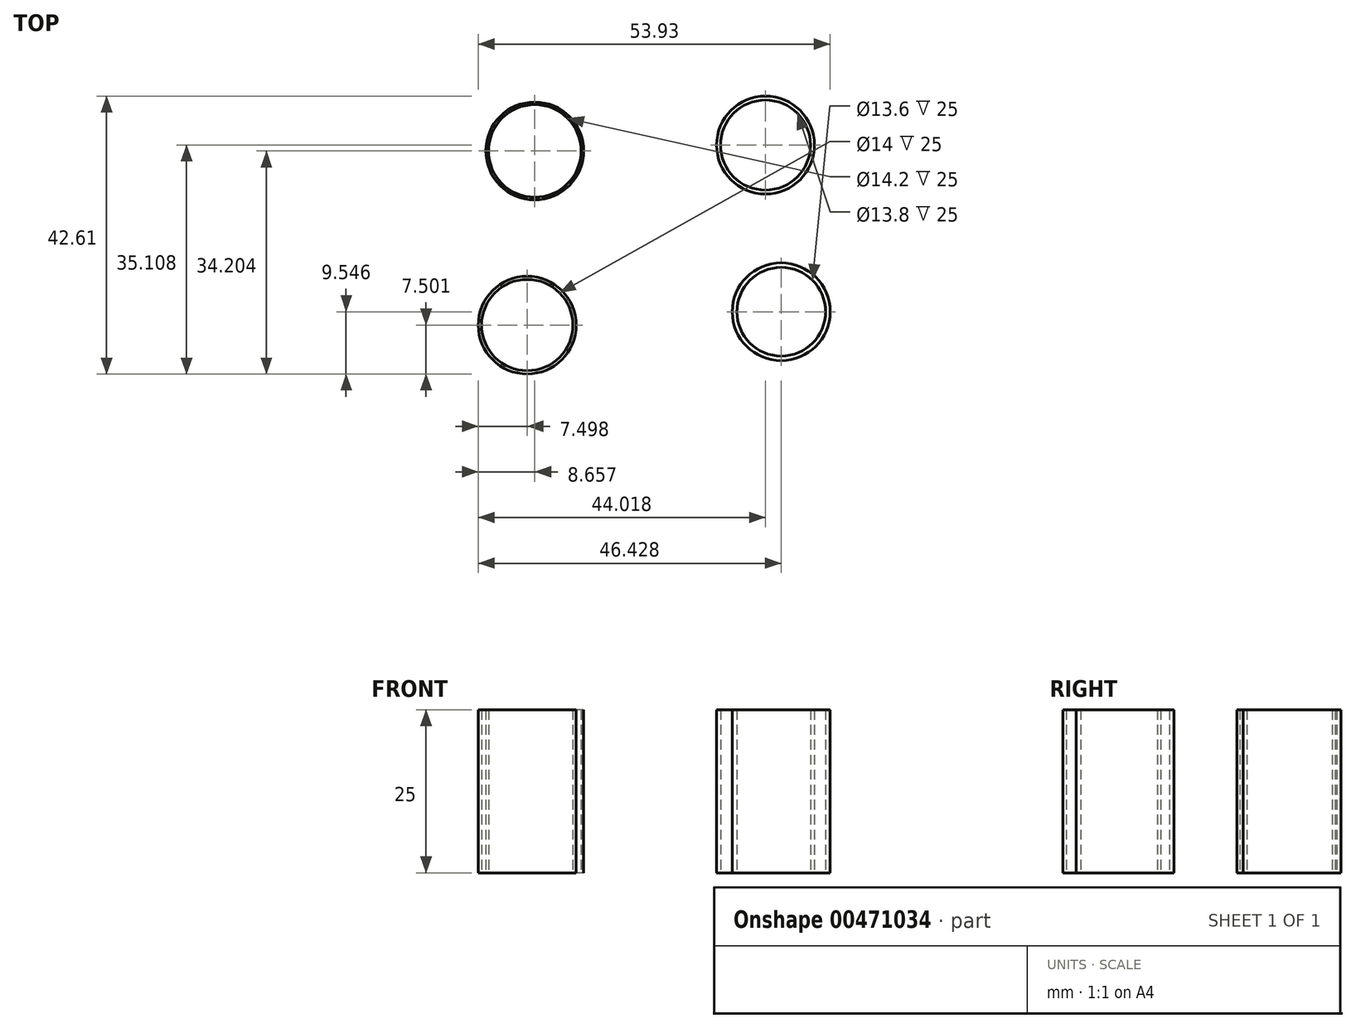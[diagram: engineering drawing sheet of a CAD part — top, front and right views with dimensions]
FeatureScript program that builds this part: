
annotation { "Feature Type Name" : "Feature", "Feature Type Description" : "" }
export const myFeature = defineFeature(function(context is Context, id is Id, definition is map)
    precondition{}
    {
        {
            var Q0;
            Q0=qCreatedBy(makeId("Top.planeOp"),FACE);
            var sketch = newSketch(context, id + "F0", { "sketchPlane" : qUnion([Q0])});
            skCircle(sketch, "E0", {"center": v(-62.66, 34.44) * mm, "radius": 7.1 * mm});
            skCircle(sketch, "E1", {"center": v(-62.66, 34.44) * mm, "radius": 7.5 * mm});
            skCircle(sketch, "E2", {"center": v(-63.82, 7.74) * mm, "radius": 7.5 * mm});
            skCircle(sketch, "E3", {"center": v(-63.82, 7.74) * mm, "radius": 7 * mm});
            skCircle(sketch, "E4", {"center": v(-27.3, 35.35) * mm, "radius": 6.9 * mm});
            skCircle(sketch, "E5", {"center": v(-27.3, 35.35) * mm, "radius": 7.5 * mm});
            skCircle(sketch, "E6", {"center": v(-24.9, 9.79) * mm, "radius": 7.5 * mm});
            skCircle(sketch, "E7", {"center": v(-24.9, 9.79) * mm, "radius": 6.8 * mm});
            skSolve(sketch);
        }
        {
            var Q0;
            Q0=makeQuery(id+"F0.imprint","IMPRINT",FACE,{"disambiguationData":[TD([[makeQuery(id+"F0.imprint","IMPRINT",EDGE,{"derivedFrom":sQuery(id+"F0.wireOp",EDGE,"E0")}),-1.0]])]});
            var Q1;
            Q1=makeQuery(id+"F0.imprint","IMPRINT",FACE,{"disambiguationData":[TD([[makeQuery(id+"F0.imprint","IMPRINT",EDGE,{"derivedFrom":sQuery(id+"F0.wireOp",EDGE,"E2")}),1.0]])]});
            var Q2;
            Q2=makeQuery(id+"F0.imprint","IMPRINT",FACE,{"disambiguationData":[TD([[makeQuery(id+"F0.imprint","IMPRINT",EDGE,{"derivedFrom":sQuery(id+"F0.wireOp",EDGE,"E4")}),-1.0]])]});
            var Q3;
            Q3=makeQuery(id+"F0.imprint","IMPRINT",FACE,{"disambiguationData":[TD([[makeQuery(id+"F0.imprint","IMPRINT",EDGE,{"derivedFrom":sQuery(id+"F0.wireOp",EDGE,"E6")}),1.0]])]});
            extrude(context, id + "F1", {"entities" : qUnion([Q0, Q1, Q2, Q3]), "depth" : 25 * mm, "offsetDistance" : 25 * mm});
        }
    });
